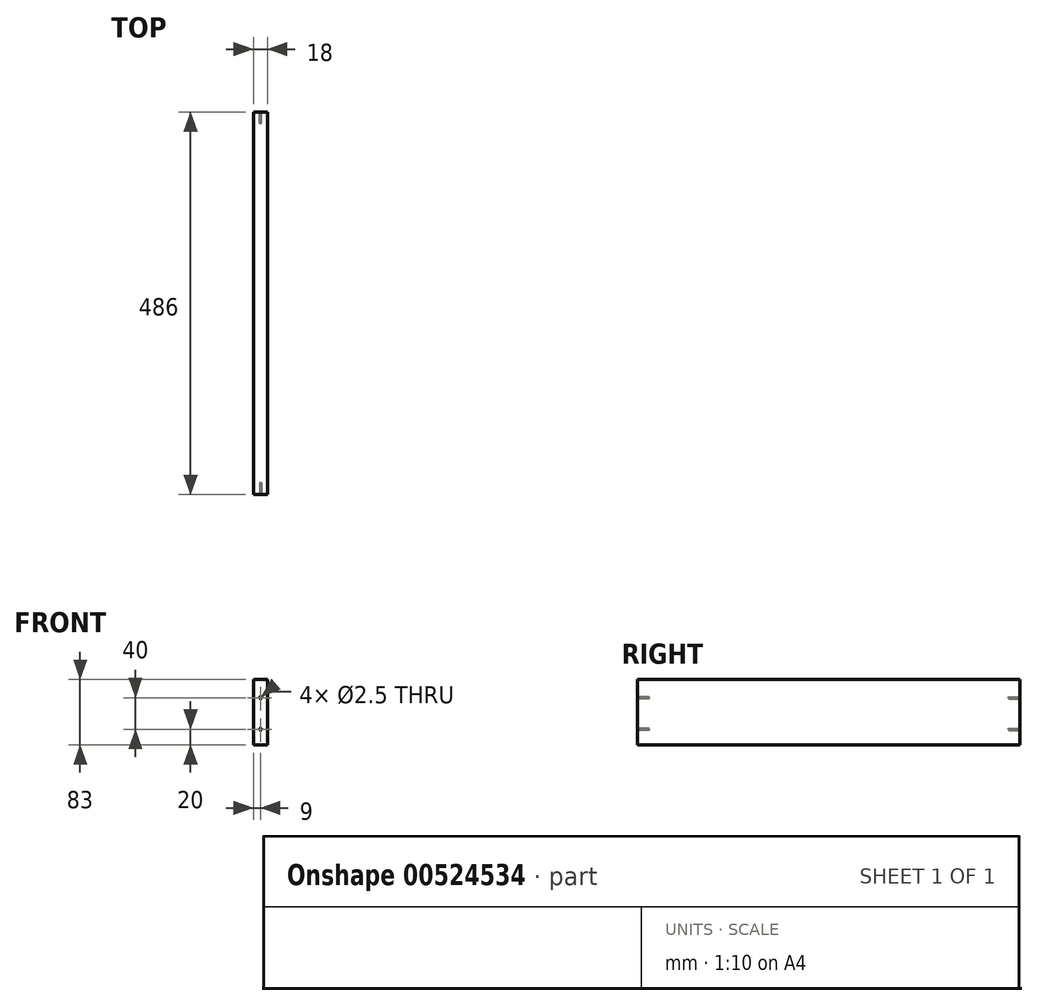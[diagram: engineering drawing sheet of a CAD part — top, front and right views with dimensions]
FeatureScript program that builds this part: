
annotation { "Feature Type Name" : "Feature", "Feature Type Description" : "" }
export const myFeature = defineFeature(function(context is Context, id is Id, definition is map)
    precondition{}
    {
        {
            var Q0;
            Q0=qCreatedBy(makeId("Right.planeOp"),FACE);
            var sketch = newSketch(context, id + "F0", { "sketchPlane" : qUnion([Q0])});
            skLineSegment(sketch, "E0.bottom", {"start": v(0, 0) * mm, "end": v(486, 0) * mm});
            skLineSegment(sketch, "E0.top", {"start": v(0, 83) * mm, "end": v(486, 83) * mm});
            skLineSegment(sketch, "E0.left", {"start": v(0, 0) * mm, "end": v(0, 83) * mm});
            skLineSegment(sketch, "E0.right", {"start": v(486, 0) * mm, "end": v(486, 83) * mm});
            skSolve(sketch);
        }
        {
            var Q0;
            Q0=qSketchRegion(id+"F0",true);
            extrude(context, id + "F1", {"entities" : qUnion([Q0]), "depth" : 18 * mm, "offsetDistance" : 25 * mm});
        }
        {
            var Q0;
            Q0=makeQuery(id+"F1.opExtrude","SWEPT_FACE",FACE,{"disambiguationData":[OSD([sQuery(id+"F0.wireOp",EDGE,"E0.left")])]});
            var sketch = newSketch(context, id + "F2", { "sketchPlane" : qUnion([Q0])});
            skPoint(sketch, "E1", {"position": v(9, 20) * mm});
            skPoint(sketch, "E2", {"position": v(9, 60) * mm});
            skSolve(sketch);
        }
        {
            var Q0;
            Q0=sQuery(id+"F2.wireOp",VERTEX,"E1");
            var Q1;
            Q1=sQuery(id+"F2.wireOp",VERTEX,"E2");
            var Q2;
            Q2=makeQuery(id+"F1.opExtrude","SWEPT_BODY",BODY,{"disambiguationData":[OSD([sQuery(id+"F0.wireOp",EDGE,"E0.bottom"),sQuery(id+"F0.wireOp",EDGE,"E0.top"),sQuery(id+"F0.wireOp",EDGE,"E0.left"),sQuery(id+"F0.wireOp",EDGE,"E0.right")])]});
            hole(context, id + "F3", {"style" : HoleStyle.SIMPLE, "endStyle" : HoleEndStyle.BLIND, "standardTappedOrClearance" : lookupTablePath({ "standard" : "ISO", "engagement" : "75%", "pitch" : "0.5 mm", "size" : "M3", "type" : "Tapped" }), "standardBlindInLast" : lookupTablePath({ "standard" : "ISO", "engagement" : "75%", "pitch" : "0.5 mm", "size" : "M3", "type" : "Tapped" }), "holeDiameter" : 2.5 * mm, "showTappedDepth" : true, "holeDepth" : 14.5 * mm, "isTappedThrough" : true, "tappedDepth" : 13 * mm, "tapClearance" : 3, "locations" : qUnion([Q0, Q1]), "scope" : qUnion([Q2]), "majorDiameter" : 3 * mm});
        }
        {
            var Q0;
            Q0=makeQuery(id+"F1.opExtrude","SWEPT_FACE",FACE,{"disambiguationData":[OSD([sQuery(id+"F0.wireOp",EDGE,"E0.right")])]});
            var sketch = newSketch(context, id + "F4", { "sketchPlane" : qUnion([Q0])});
            skPoint(sketch, "E3", {"position": v(-9, 20) * mm});
            skPoint(sketch, "E4", {"position": v(-9, 60) * mm});
            skSolve(sketch);
        }
        {
            var Q0;
            Q0=sQuery(id+"F4.wireOp",VERTEX,"E4");
            var Q1;
            Q1=sQuery(id+"F4.wireOp",VERTEX,"E3");
            var Q2;
            Q2=makeQuery(id+"F1.opExtrude","SWEPT_BODY",BODY,{"disambiguationData":[OSD([sQuery(id+"F0.wireOp",EDGE,"E0.bottom"),sQuery(id+"F0.wireOp",EDGE,"E0.top"),sQuery(id+"F0.wireOp",EDGE,"E0.left"),sQuery(id+"F0.wireOp",EDGE,"E0.right")])]});
            hole(context, id + "F5", {"style" : HoleStyle.SIMPLE, "endStyle" : HoleEndStyle.BLIND, "standardTappedOrClearance" : lookupTablePath({ "standard" : "ISO", "engagement" : "75%", "pitch" : "0.5 mm", "size" : "M3", "type" : "Tapped" }), "standardBlindInLast" : lookupTablePath({ "standard" : "ISO", "engagement" : "75%", "pitch" : "0.5 mm", "size" : "M3", "type" : "Tapped" }), "holeDiameter" : 2.5 * mm, "showTappedDepth" : true, "holeDepth" : 14 * mm, "isTappedThrough" : true, "tappedDepth" : 12.5 * mm, "tapClearance" : 3, "locations" : qUnion([Q0, Q1]), "scope" : qUnion([Q2]), "majorDiameter" : 3 * mm});
        }
    });
